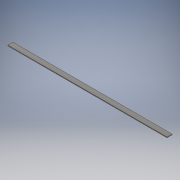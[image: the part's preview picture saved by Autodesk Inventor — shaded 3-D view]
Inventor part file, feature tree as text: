
AUTODESK INVENTOR PART (.ipt)
format: ipt  version: 2018 (Build 220112000, 112)  size: 95,232 bytes
history: native  units: mm
features: extrude x1, sketch x1
ambient origin geometry x8: Origin, YZ Plane, XZ Plane, XY Plane, X Axis, Y Axis, Z Axis, Center Point
bodies: Solid1 (feature_tree)
feature tree (2):
  extrude  "Extrusion1"  Depth=6.0mm
  sketch  "Sketch1"  dims[d0=38.1mm d1=6.0mm d2=1200.0mm d3=0.0mm]
